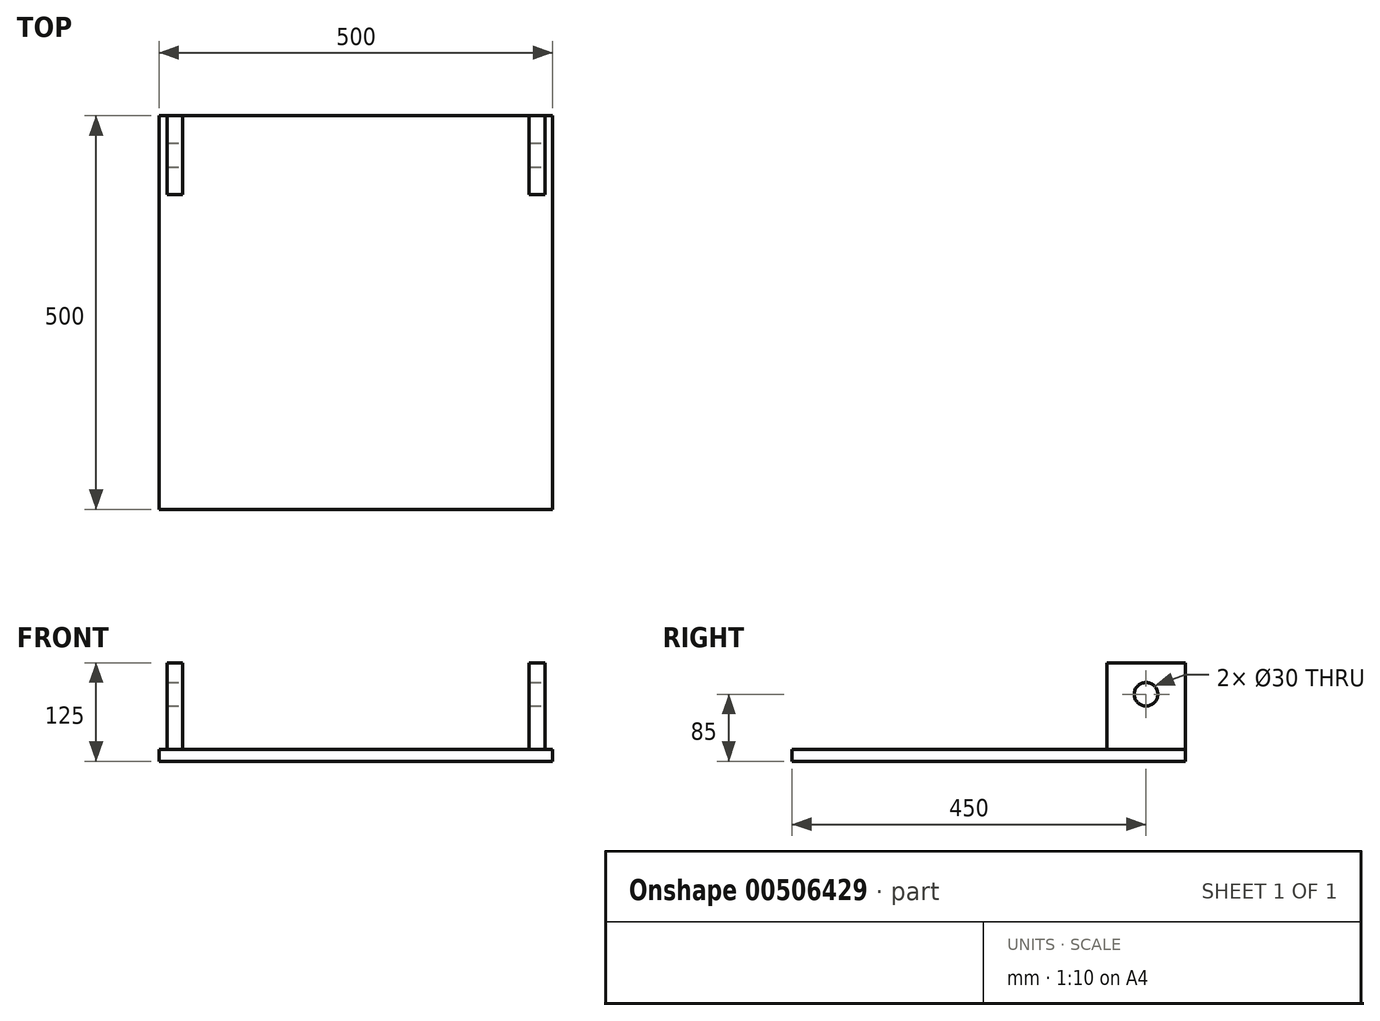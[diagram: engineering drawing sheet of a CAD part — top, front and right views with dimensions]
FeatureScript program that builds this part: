
annotation { "Feature Type Name" : "Feature", "Feature Type Description" : "" }
export const myFeature = defineFeature(function(context is Context, id is Id, definition is map)
    precondition{}
    {
        {
            var Q0;
            Q0=qCreatedBy(makeId("Top.planeOp"),FACE);
            var sketch = newSketch(context, id + "F0", { "sketchPlane" : qUnion([Q0])});
            skLineSegment(sketch, "E0.bottom", {"start": v(250, -250) * mm, "end": v(-250, -250) * mm});
            skLineSegment(sketch, "E0.top", {"start": v(250, 250) * mm, "end": v(-250, 250) * mm});
            skLineSegment(sketch, "E0.left", {"start": v(250, -250) * mm, "end": v(250, 250) * mm});
            skLineSegment(sketch, "E0.right", {"start": v(-250, -250) * mm, "end": v(-250, 250) * mm});
            skPoint(sketch, "E0.middle", {"position": v(0, 0) * mm});
            skSolve(sketch);
        }
        {
            var Q0;
            Q0=makeQuery(id+"F0.imprint","IMPRINT",FACE,{"disambiguationData":[TD([[makeQuery(id+"F0.imprint","IMPRINT",EDGE,{"derivedFrom":sQuery(id+"F0.wireOp",EDGE,"E0.bottom")}),-1.0]])]});
            extrude(context, id + "F1", {"entities" : qUnion([Q0]), "depth" : 15 * mm});
        }
        {
            var Q0;
            Q0=makeQuery(id+"F1.opExtrude","CAP_FACE",FACE,{"disambiguationData":[OSD([sQuery(id+"F0.wireOp",EDGE,"E0.bottom"),sQuery(id+"F0.wireOp",EDGE,"E0.top"),sQuery(id+"F0.wireOp",EDGE,"E0.left"),sQuery(id+"F0.wireOp",EDGE,"E0.right")])],"isStart":false});
            var sketch = newSketch(context, id + "F2", { "sketchPlane" : qUnion([Q0])});
            skLineSegment(sketch, "E1.bottom", {"start": v(240, 150) * mm, "end": v(220, 150) * mm});
            skLineSegment(sketch, "E1.top", {"start": v(240, 250) * mm, "end": v(220, 250) * mm});
            skLineSegment(sketch, "E1.left", {"start": v(240, 150) * mm, "end": v(240, 250) * mm});
            skLineSegment(sketch, "E1.right", {"start": v(220, 150) * mm, "end": v(220, 250) * mm});
            skPoint(sketch, "E1.middle", {"position": v(230, 200) * mm});
            skLineSegment(sketch, "E2", {"start": v(0, 0) * mm, "end": v(0, 448.85) * mm});
            skLineSegment(sketch, "E3.MirrorCS", {"start": v(-220, 150) * mm, "end": v(-220, 250) * mm});
            skLineSegment(sketch, "E4.MirrorCS", {"start": v(-240, 150) * mm, "end": v(-220, 150) * mm});
            skLineSegment(sketch, "E5.MirrorCS", {"start": v(-240, 150) * mm, "end": v(-240, 250) * mm});
            skLineSegment(sketch, "E6.MirrorCS", {"start": v(-240, 250) * mm, "end": v(-220, 250) * mm});
            skSolve(sketch);
        }
        {
            var Q0;
            Q0 = qSketchRegion(id + "F2", true);
            extrude(context, id + "F3", {"entities" : qUnion([Q0]), "operationType" : NewBodyOperationType.ADD, "depth" : 110 * mm});
        }
        {
            var Q0;
            Q0=makeQuery(id+"F3.opExtrude","SWEPT_FACE",FACE,{"disambiguationData":[OSD([sQuery(id+"F2.wireOp",EDGE,"E1.left")])]});
            var sketch = newSketch(context, id + "F4", { "sketchPlane" : qUnion([Q0])});
            skCircle(sketch, "E7", {"center": v(200, 85) * mm, "radius": 15 * mm});
            skSolve(sketch);
        }
        {
            var Q0;
            Q0 = qSketchRegion(id + "F4", true);
            var Q1;
            Q1=makeQuery(id+"F4.imprint","IMPRINT",FACE,{"disambiguationData":[TD([[makeQuery(id+"F4.imprint","IMPRINT",EDGE,{"derivedFrom":sQuery(id+"F4.wireOp",EDGE,"E7")}),1.0]])]});
            extrude(context, id + "F5", {"entities" : qUnion([Q0, Q1]), "operationType" : NewBodyOperationType.REMOVE, "endBound" : BoundingType.THROUGH_ALL, "oppositeDirection" : true, "depth" : 25 * mm});
        }
    });
